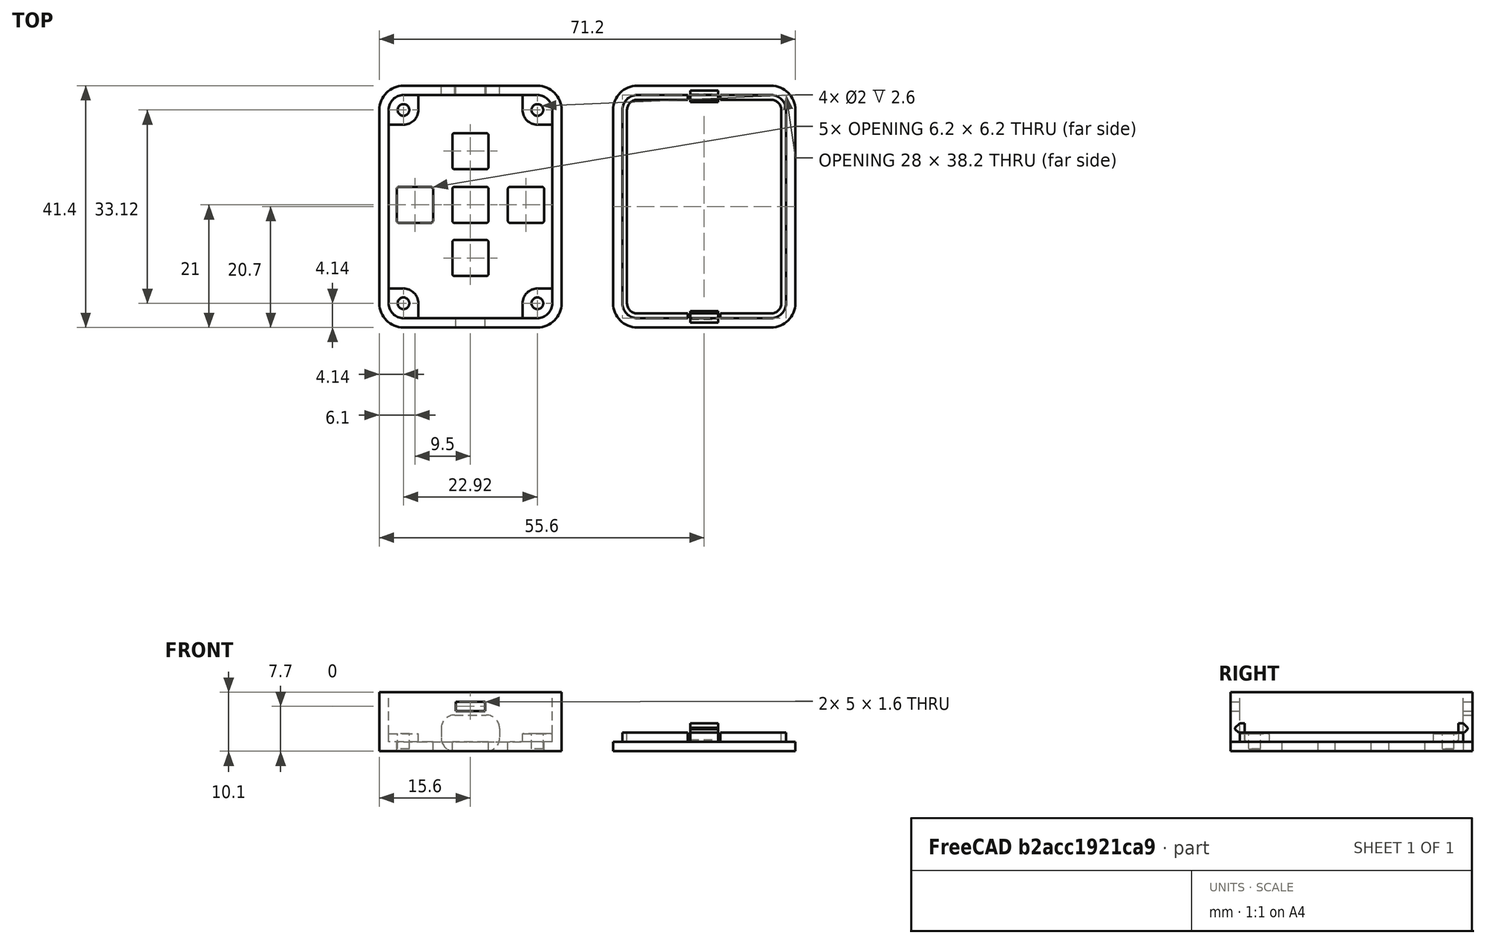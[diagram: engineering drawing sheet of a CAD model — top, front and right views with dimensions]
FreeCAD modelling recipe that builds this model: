
FCSTD DOCUMENT  (FreeCAD 0.16R)
Label: TinyRemoteIR
License: All rights reserved
LicenseURL: http://en.wikipedia.org/wiki/All_rights_reserved
objects: Part::Box×21, Part::Fillet×12, Part::Cut×7, Part::MultiFuse×6, Part::Chamfer×5, Part::Cylinder×4
note: 55 computed .brp shape members not serialized (recipe doc carries the construction recipe); baked Part::Feature solids carry a one-line shape summary decoded from their .brp

FEATURE [Part::Box] Box  label="Würfel"
  Height = 10.1
  Length = 31.2
  Placement = pos=(-1.6,-1.6,0) rot=(0,0,1;0rad)
  Width = 41.4
FEATURE [Part::Box] Box001  label="Würfel001"
  Height = 10
  Length = 28
  Placement = pos=(0,0,1.6) rot=(0,0,1;0rad)
  Width = 38.2
FEATURE [Part::Cut] Cut
  Base = -> Box
  Tool = -> Box001
FEATURE [Part::Box] Box002  label="Würfel002"
  Height = 3
  Length = 5.08
  Width = 5.08
FEATURE [Part::Box] Box003  label="Würfel003"
  Height = 3
  Length = 5.08
  Placement = pos=(22.92,0,0) rot=(0,0,1;0rad)
  Width = 5.08
FEATURE [Part::Box] Box004  label="Würfel004"
  Height = 3
  Length = 5.08
  Placement = pos=(0,33.12,0) rot=(0,0,1;0rad)
  Width = 5.08
FEATURE [Part::Box] Box005  label="Würfel005"
  Height = 3
  Length = 5.08
  Placement = pos=(22.92,33.12,0) rot=(0,0,1;0rad)
  Width = 5.08
FEATURE [Part::MultiFuse] Fusion
  Shapes = -> [Cut,Box002,Box003,Box004,Box005]
FEATURE [Part::Fillet] Fillet
  Base = -> Fusion
  Edges = 4 edges r=2.54: [Edge59,Edge69,Edge73,Edge74]
FEATURE [Part::Fillet] Fillet001
  Base = -> Fillet
  Edges = 4 edges r=2.54: [Edge11,Edge13,Edge19,Edge41]
FEATURE [Part::Fillet] Fillet002
  Base = -> Fillet001
  Edges = 4 edges r=4.14: [Edge70,Edge71,Edge74,Edge76]
FEATURE [Part::Cylinder] Cylinder  label="Zylinder"
  Angle = 360
  Height = 10
  Placement = pos=(2.54,2.54,0.4) rot=(0,0,1;0rad)
  Radius = 1
FEATURE [Part::Cylinder] Cylinder001  label="Zylinder001"
  Angle = 360
  Height = 10
  Placement = pos=(25.46,2.54,0.4) rot=(0,0,1;0rad)
  Radius = 1
FEATURE [Part::Cylinder] Cylinder002  label="Zylinder002"
  Angle = 360
  Height = 10
  Placement = pos=(2.54,35.66,0.4) rot=(0,0,1;0rad)
  Radius = 1
FEATURE [Part::Cylinder] Cylinder003  label="Zylinder003"
  Angle = 360
  Height = 10
  Placement = pos=(25.46,35.66,0.4) rot=(0,0,1;0rad)
  Radius = 1
FEATURE [Part::MultiFuse] Fusion001
  Shapes = -> [Cylinder,Cylinder003,Cylinder002,Cylinder001]
FEATURE [Part::Cut] Cut001  label="Case_raw"
  Base = -> Fillet002
  Tool = -> Fusion001
FEATURE [Part::Box] Box006  label="Würfel006"
  Height = 2
  Length = 6.2
  Placement = pos=(10.9,7.2,0) rot=(0,0,1;0rad)
  Width = 6.2
FEATURE [Part::Box] Box007  label="Würfel007"
  Height = 2
  Length = 6.2
  Placement = pos=(10.9,16.3,0) rot=(0,0,1;0rad)
  Width = 6.2
FEATURE [Part::Box] Box008  label="Würfel008"
  Height = 2
  Length = 6.2
  Placement = pos=(10.9,25.5,0) rot=(0,0,1;0rad)
  Width = 6.2
FEATURE [Part::Box] Box009  label="Würfel009"
  Height = 2
  Length = 6.2
  Placement = pos=(1.4,16.3,0) rot=(0,0,1;0rad)
  Width = 6.2
FEATURE [Part::Box] Box010  label="Würfel010"
  Height = 2
  Length = 6.2
  Placement = pos=(20.4,16.3,0) rot=(0,0,1;0rad)
  Width = 6.2
FEATURE [Part::Fillet] Fillet003
  Base = -> Box008
  Edges = 4 edges r=0.4: [Edge1,Edge3,Edge5,Edge7]
FEATURE [Part::Fillet] Fillet004
  Base = -> Box009
  Edges = 4 edges r=0.4: [Edge1,Edge3,Edge5,Edge7]
FEATURE [Part::Fillet] Fillet005
  Base = -> Box007
  Edges = 4 edges r=0.4: [Edge1,Edge3,Edge5,Edge7]
FEATURE [Part::Fillet] Fillet006
  Base = -> Box010
  Edges = 4 edges r=0.4: [Edge1,Edge3,Edge5,Edge7]
FEATURE [Part::Fillet] Fillet007
  Base = -> Box006
  Edges = 4 edges r=0.4: [Edge1,Edge3,Edge5,Edge7]
FEATURE [Part::MultiFuse] Fusion002  label="Buttons"
  Shapes = -> [Fillet003,Fillet004,Fillet005,Fillet006,Fillet007]
FEATURE [Part::Box] Box011  label="Würfel011"
  Height = 6.2
  Length = 10
  Placement = pos=(9,38.2,0) rot=(0,0,1;0rad)
  Width = 3.2
FEATURE [Part::Fillet] Fillet008  label="LED"
  Base = -> Box011
  Edges = 4 edges r=2.29: [Edge2,Edge4,Edge6,Edge8]
FEATURE [Part::Box] Box012  label="Würfel012"
  Height = 1.6
  Length = 5
  Placement = pos=(11.5,-1.6,6.9) rot=(0,0,1;0rad)
  Width = 1.6
FEATURE [Part::Box] Box013  label="Würfel013"
  Height = 1.6
  Length = 5
  Placement = pos=(11.5,38.2,6.9) rot=(0,0,1;0rad)
  Width = 1.6
FEATURE [Part::MultiFuse] Fusion003  label="Nut"
  Shapes = -> [Box012,Box013]
FEATURE [Part::Box] Box014  label="Würfel014"
  Height = 1.6
  Length = 31.2
  Placement = pos=(38.4,-1.6,0) rot=(0,0,1;0rad)
  Width = 41.4
FEATURE [Part::Box] Box015  label="Würfel015"
  Height = 3.2
  Length = 28
  Placement = pos=(40,0,0) rot=(0,0,1;0rad)
  Width = 38.2
FEATURE [Part::Box] Box016  label="Würfel016"
  Height = 1.6
  Length = 26.4
  Placement = pos=(40.8,0.8,1.6) rot=(0,0,1;0rad)
  Width = 36.6
FEATURE [Part::Cut] Cut002
  Base = -> Box015
  Tool = -> Box016
FEATURE [Part::Fillet] Fillet009
  Base = -> Cut002
  Edges = 4 edges r=1.74: [Edge17,Edge19,Edge21,Edge22]
FEATURE [Part::Fillet] Fillet010
  Base = -> Fillet009
  Edges = 4 edges r=2.54: [Edge29,Edge30,Edge33,Edge35]
FEATURE [Part::Fillet] Fillet011
  Base = -> Box014
  Edges = 4 edges r=4.14: [Edge1,Edge3,Edge5,Edge7]
FEATURE [Part::Box] Box017  label="Würfel017"
  Height = 1.6
  Length = 4.8
  Placement = pos=(51.6,-0.8,3.2) rot=(0,0,1;0rad)
  Width = 1.6
FEATURE [Part::Box] Box018  label="Würfel018"
  Height = 1.6
  Length = 4.8
  Placement = pos=(51.6,37.4,3.2) rot=(0,0,1;0rad)
  Width = 1.6
FEATURE [Part::Chamfer] Chamfer
  Base = -> Box017
  Edges = 1 edges r=0.8: [Edge10]
FEATURE [Part::Chamfer] Chamfer001
  Base = -> Chamfer
  Edges = 1 edges r=0.6: [Edge8]
FEATURE [Part::Chamfer] Chamfer002
  Base = -> Box018
  Edges = 1 edges r=0.8: [Edge12]
FEATURE [Part::Chamfer] Chamfer003
  Base = -> Chamfer002
  Edges = 1 edges r=0.6: [Edge14]
FEATURE [Part::MultiFuse] Fusion004  label="Lid_raw"
  Shapes = -> [Fillet010,Fillet011,Chamfer001,Chamfer003]
FEATURE [Part::Cut] Cut003
  Base = -> Cut001
  Tool = -> Fusion002
FEATURE [Part::Cut] Cut004
  Base = -> Cut003
  Tool = -> Fusion003
FEATURE [Part::Cut] Cut005  label="Case"
  Base = -> Cut004
  Tool = -> Fillet008
FEATURE [Part::Box] Box019  label="Würfel019"
  Height = 1.6
  Length = 0.4
  Placement = pos=(51.2,0,1.6) rot=(0,0,1;0rad)
  Width = 38.2
FEATURE [Part::Box] Box020  label="Würfel020"
  Height = 1.6
  Length = 0.4
  Placement = pos=(56.4,0,1.6) rot=(0,0,1;0rad)
  Width = 38.2
FEATURE [Part::MultiFuse] Fusion005  label="Lid_Nut"
  Shapes = -> [Box019,Box020]
FEATURE [Part::Cut] Cut006  label="Lid_raw001"
  Base = -> Fusion004
  Tool = -> Fusion005
FEATURE [Part::Chamfer] Chamfer004  label="Lid"
  Base = -> Cut006
  Edges = 2 edges r=0.4: [Edge134,Edge141]
